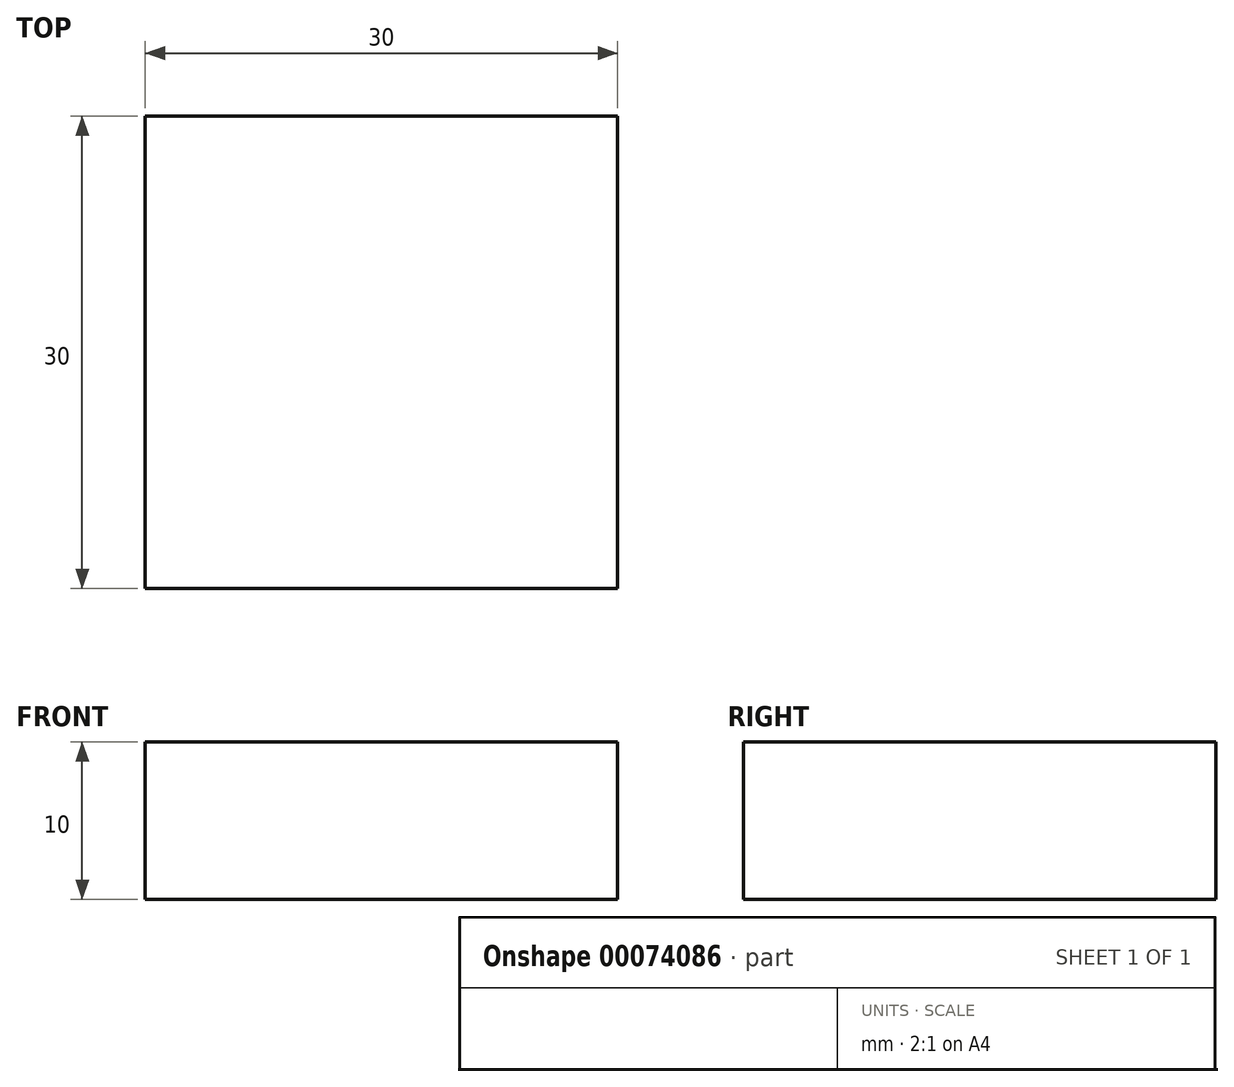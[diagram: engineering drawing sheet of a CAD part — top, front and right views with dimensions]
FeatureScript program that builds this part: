
annotation { "Feature Type Name" : "Feature", "Feature Type Description" : "" }
export const myFeature = defineFeature(function(context is Context, id is Id, definition is map)
    precondition{}
    {
        {
            var Q0;
            Q0=qCreatedBy(makeId("Top.planeOp"),FACE);
            var sketch = newSketch(context, id + "F0", { "sketchPlane" : qUnion([Q0])});
            skLineSegment(sketch, "E0.rect.bottom", {"start": v(-15, 15) * mm, "end": v(15, 15) * mm});
            skLineSegment(sketch, "E0.rect.top", {"start": v(-15, -15) * mm, "end": v(15, -15) * mm});
            skLineSegment(sketch, "E0.rect.left", {"start": v(-15, 15) * mm, "end": v(-15, -15) * mm});
            skLineSegment(sketch, "E0.rect.right", {"start": v(15, 15) * mm, "end": v(15, -15) * mm});
            skPoint(sketch, "E0.rect.middle", {"position": v(0, 0) * mm});
            skSolve(sketch);
        }
        {
            var Q0;
            Q0 = qSketchRegion(id + "F0", true);
            extrude(context, id + "F1", {"entities" : qUnion([Q0]), "depth" : 10 * mm});
        }
    });
